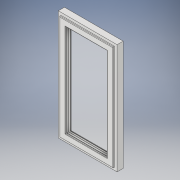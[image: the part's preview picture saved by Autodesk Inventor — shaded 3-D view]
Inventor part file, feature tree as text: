
AUTODESK INVENTOR PART (.ipt)
format: ipt  version: 2019 (Build 230136000, 136)  size: 202,752 bytes
history: native  units: mm
features: other x6, sketch x3, sweep x2, extrude x1, pattern_linear x1, projected_geometry x1
ambient origin geometry x8: Origin, YZ Plane, XZ Plane, XY Plane, X Axis, Y Axis, Z Axis, Center Point
bodies: Body1 (feature_tree), Body2 (feature_tree), Body3 (feature_tree)
feature tree (14):
  other  "Таблица"
  other  "Окно-01"
  other  "Окно-02"
  other  "Обвязка"
  sketch  "Эскиз2"
  sketch  "Эскиз1"
  sweep  "Сдвиг1"
  sweep  "Сдвиг2"
  extrude  "Выдавливание1"  Depth=10.0mm TaperAngle=0.0deg
  pattern_linear  "Прямоуг.массив1"  Count1=3 Spacing1=21.5mm
  sketch  "Эскиз3"
  other  "Рама"
  projected_geometry  "Спроецированная петля2"
  other  "Стекло"
